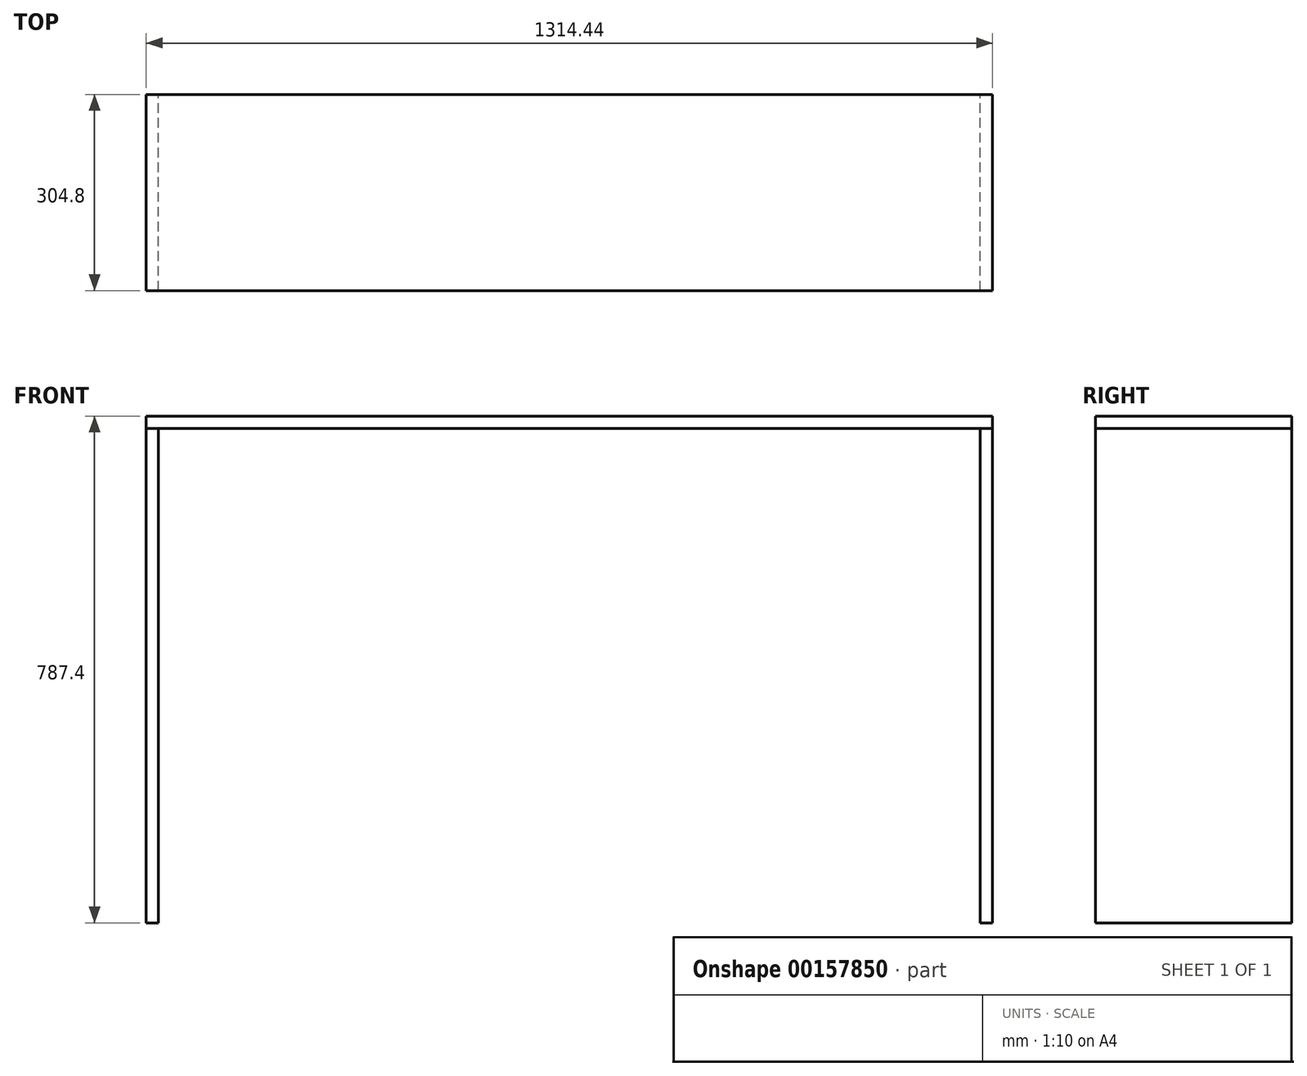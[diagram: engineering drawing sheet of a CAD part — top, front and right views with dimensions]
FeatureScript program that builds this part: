
annotation { "Feature Type Name" : "Feature", "Feature Type Description" : "" }
export const myFeature = defineFeature(function(context is Context, id is Id, definition is map)
    precondition{}
    {
        {
            var Q0;
            Q0=qCreatedBy(makeId("Top.planeOp"),FACE);
            var sketch = newSketch(context, id + "F0", { "sketchPlane" : qUnion([Q0])});
            skLineSegment(sketch, "E0.bottom", {"start": v(-657.23, 152.4) * mm, "end": v(657.23, 152.4) * mm});
            skLineSegment(sketch, "E0.top", {"start": v(-657.23, -152.4) * mm, "end": v(657.23, -152.4) * mm});
            skLineSegment(sketch, "E0.left", {"start": v(-657.23, 152.4) * mm, "end": v(-657.23, -152.4) * mm});
            skLineSegment(sketch, "E0.right", {"start": v(657.23, 152.4) * mm, "end": v(657.23, -152.4) * mm});
            skPoint(sketch, "E0.middle", {"position": v(0, 0) * mm});
            skSolve(sketch);
        }
        {
            var Q0;
            Q0 = qSketchRegion(id + "F0", true);
            extrude(context, id + "F1", {"entities" : qUnion([Q0]), "depth" : 19.05 * mm});
        }
        {
            var Q0;
            Q0=makeQuery(id+"F1.opExtrude","SWEPT_FACE",FACE,{"disambiguationData":[OSD([sQuery(id+"F0.wireOp",EDGE,"E0.bottom")])]});
            var sketch = newSketch(context, id + "F2", { "sketchPlane" : qUnion([Q0])});
            skLineSegment(sketch, "E1.bottom", {"start": v(-657.23, 0) * mm, "end": v(-638.17, 0) * mm});
            skLineSegment(sketch, "E1.top", {"start": v(-657.23, -768.35) * mm, "end": v(-638.17, -768.35) * mm});
            skLineSegment(sketch, "E1.left", {"start": v(-657.23, 0) * mm, "end": v(-657.23, -768.35) * mm});
            skLineSegment(sketch, "E1.right", {"start": v(-638.17, 0) * mm, "end": v(-638.17, -768.35) * mm});
            skLineSegment(sketch, "E2.bottom", {"start": v(638.18, 0) * mm, "end": v(657.23, 0) * mm});
            skLineSegment(sketch, "E2.top", {"start": v(638.18, -768.35) * mm, "end": v(657.23, -768.35) * mm});
            skLineSegment(sketch, "E2.left", {"start": v(638.18, 0) * mm, "end": v(638.18, -768.35) * mm});
            skLineSegment(sketch, "E2.right", {"start": v(657.23, 0) * mm, "end": v(657.23, -768.35) * mm});
            skSolve(sketch);
        }
        {
            var Q0;
            Q0 = qSketchRegion(id + "F2", true);
            extrude(context, id + "F3", {"entities" : qUnion([Q0]), "oppositeDirection" : true, "depth" : 304.8 * mm});
        }
    });
